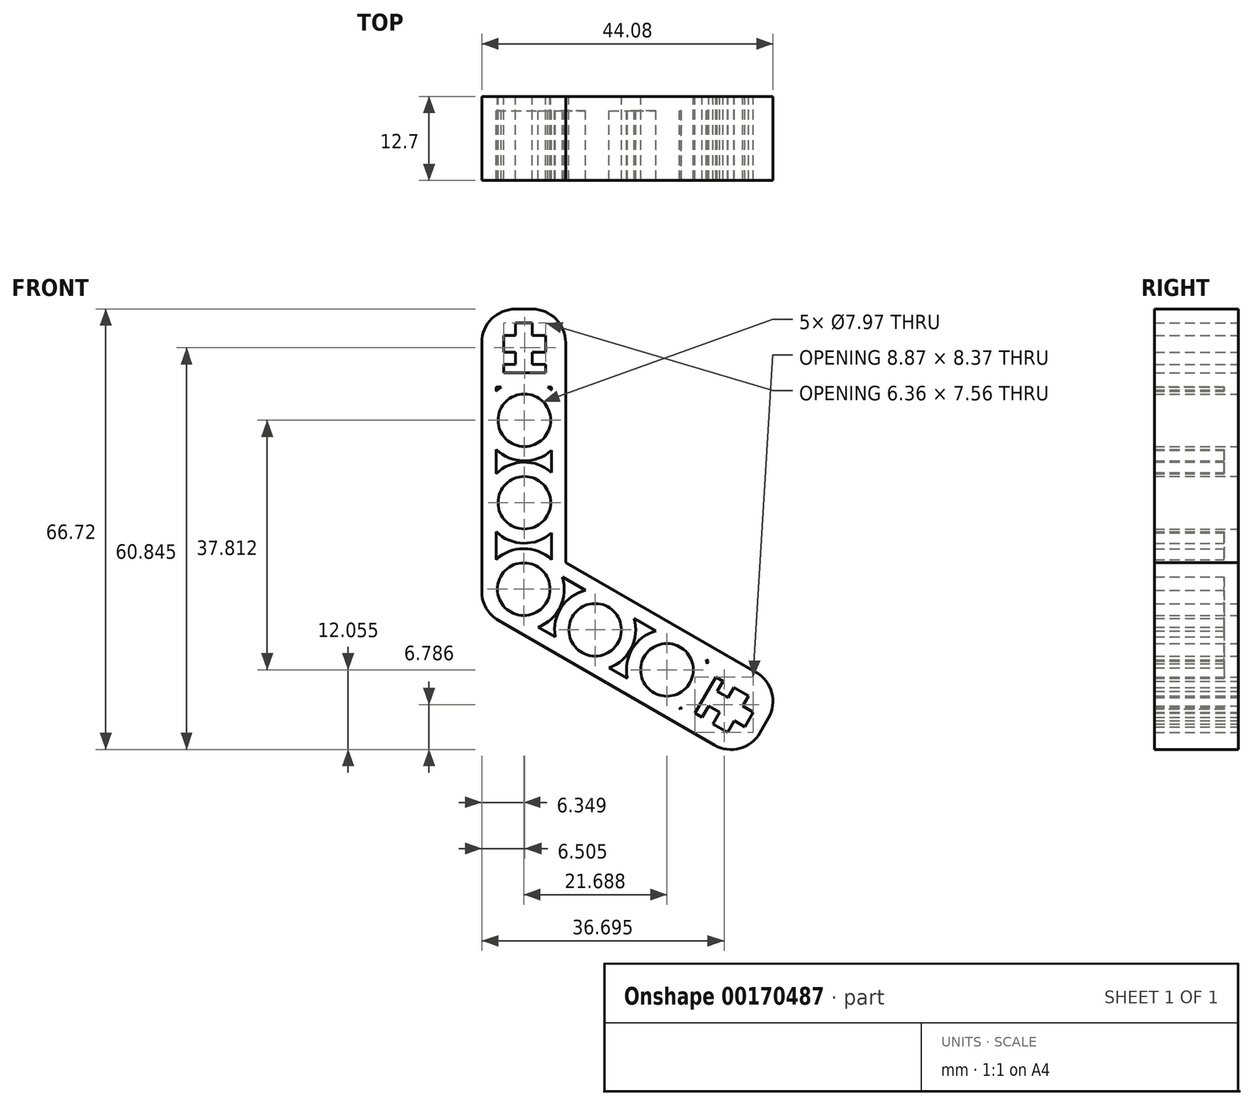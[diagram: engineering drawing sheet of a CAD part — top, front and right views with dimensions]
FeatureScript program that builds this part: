
annotation { "Feature Type Name" : "Feature", "Feature Type Description" : "" }
export const myFeature = defineFeature(function(context is Context, id is Id, definition is map)
    precondition{}
    {
        {
            var Q0;
            Q0=qCreatedBy(makeId("Front.planeOp"),FACE);
            var sketch = newSketch(context, id + "F0", { "sketchPlane" : qUnion([Q0])});
            skLineSegment(sketch, "E0.bottom", {"start": v(-54.24, 38.39) * mm, "end": v(-41.54, 38.39) * mm});
            skLineSegment(sketch, "E0.left", {"start": v(-54.24, 38.39) * mm, "end": v(-54.24, -7.33) * mm});
            skLineSegment(sketch, "E0.right", {"start": v(-41.54, 38.39) * mm, "end": v(-41.54, 0) * mm});
            skLineSegment(sketch, "E1.top", {"start": v(-14.65, -30.2) * mm, "end": v(-8.3, -19.2) * mm});
            skLineSegment(sketch, "E1.left", {"start": v(-54.24, -7.33) * mm, "end": v(-14.65, -30.2) * mm});
            skLineSegment(sketch, "E1.right", {"start": v(-41.54, 0) * mm, "end": v(-8.3, -19.2) * mm});
            skCircle(sketch, "E2", {"center": v(-47.9, -4.05) * mm, "radius": 3.98 * mm});
            skLineSegment(sketch, "E3.bottom", {"start": v(-16.05, -18.96) * mm, "end": v(-13.85, -20.24) * mm});
            skLineSegment(sketch, "E3.top", {"start": v(-19.23, -24.46) * mm, "end": v(-17.04, -25.73) * mm});
            skLineSegment(sketch, "E3.left", {"start": v(-16.05, -18.96) * mm, "end": v(-19.23, -24.46) * mm});
            skLineSegment(sketch, "E3.right", {"start": v(-13.85, -20.24) * mm, "end": v(-17.04, -25.73) * mm});
            skLineSegment(sketch, "E4.bottom", {"start": v(-19.88, -21.73) * mm, "end": v(-18.6, -19.53) * mm});
            skLineSegment(sketch, "E4.top", {"start": v(-14.39, -24.91) * mm, "end": v(-13.11, -22.72) * mm});
            skLineSegment(sketch, "E4.left", {"start": v(-19.88, -21.73) * mm, "end": v(-14.39, -24.91) * mm});
            skLineSegment(sketch, "E4.right", {"start": v(-18.6, -19.53) * mm, "end": v(-13.11, -22.72) * mm});
            skLineSegment(sketch, "E5.bottom", {"start": v(-18.8, -17.36) * mm, "end": v(-17.7, -18) * mm});
            skLineSegment(sketch, "E5.top", {"start": v(-21.98, -22.85) * mm, "end": v(-20.88, -23.49) * mm});
            skLineSegment(sketch, "E5.left", {"start": v(-18.8, -17.36) * mm, "end": v(-21.98, -22.85) * mm});
            skLineSegment(sketch, "E5.right", {"start": v(-17.7, -18) * mm, "end": v(-20.88, -23.49) * mm});
            skLineSegment(sketch, "E6.bottom", {"start": v(-50.92, 31.87) * mm, "end": v(-50.9, 34.41) * mm});
            skLineSegment(sketch, "E6.top", {"start": v(-44.57, 31.86) * mm, "end": v(-44.56, 34.4) * mm});
            skLineSegment(sketch, "E6.left", {"start": v(-50.92, 31.87) * mm, "end": v(-44.57, 31.86) * mm});
            skLineSegment(sketch, "E6.right", {"start": v(-50.9, 34.41) * mm, "end": v(-44.56, 34.4) * mm});
            skLineSegment(sketch, "E7.bottom", {"start": v(-46.6, 30.02) * mm, "end": v(-49.15, 30.03) * mm});
            skLineSegment(sketch, "E7.top", {"start": v(-46.6, 36.29) * mm, "end": v(-49.13, 36.3) * mm});
            skLineSegment(sketch, "E7.left", {"start": v(-46.6, 30.02) * mm, "end": v(-46.6, 36.29) * mm});
            skLineSegment(sketch, "E7.right", {"start": v(-49.15, 30.03) * mm, "end": v(-49.13, 36.3) * mm});
            skLineSegment(sketch, "E8.bottom", {"start": v(-50.9, 28.75) * mm, "end": v(-50.9, 30.03) * mm});
            skLineSegment(sketch, "E8.top", {"start": v(-44.56, 28.74) * mm, "end": v(-44.55, 30.02) * mm});
            skLineSegment(sketch, "E8.left", {"start": v(-50.9, 28.75) * mm, "end": v(-44.56, 28.74) * mm});
            skLineSegment(sketch, "E8.right", {"start": v(-50.9, 30.03) * mm, "end": v(-44.55, 30.02) * mm});
            skCircle(sketch, "E9", {"center": v(-37.08, -10.2) * mm, "radius": 3.98 * mm});
            skCircle(sketch, "E10", {"center": v(-47.8, 9.05) * mm, "radius": 3.98 * mm});
            skCircle(sketch, "E11", {"center": v(-47.8, 21.54) * mm, "radius": 3.98 * mm});
            skCircle(sketch, "E12", {"center": v(-26.2, -16.28) * mm, "radius": 3.98 * mm});
            skCircle(sketch, "E13", {"center": v(-47.8, 21.54) * mm, "radius": 4.75 * mm});
            skCircle(sketch, "E14", {"center": v(-47.8, 9.05) * mm, "radius": 4.75 * mm});
            skCircle(sketch, "E15", {"center": v(-47.9, -4.05) * mm, "radius": 4.75 * mm});
            skCircle(sketch, "E16", {"center": v(-37.08, -10.2) * mm, "radius": 4.75 * mm});
            skCircle(sketch, "E17", {"center": v(-26.2, -16.28) * mm, "radius": 4.75 * mm});
            skSolve(sketch);
        }
        {
            var Q0;
            Q0=makeQuery(id+"F0.imprint","IMPRINT",FACE,{"disambiguationData":[TD([[makeQuery(id+"F0.imprint","IMPRINT",EDGE,{"derivedFrom":sQuery(id+"F0.wireOp",EDGE,"E11")}),-1.0]])]});
            var Q1;
            Q1=makeQuery(id+"F0.imprint","IMPRINT",FACE,{"disambiguationData":[TD([[makeQuery(id+"F0.imprint","IMPRINT",EDGE,{"derivedFrom":sQuery(id+"F0.wireOp",EDGE,"E10")}),-1.0]])]});
            var Q2;
            Q2=makeQuery(id+"F0.imprint","IMPRINT",FACE,{"disambiguationData":[TD([[makeQuery(id+"F0.imprint","IMPRINT",EDGE,{"derivedFrom":sQuery(id+"F0.wireOp",EDGE,"E2")}),-1.0]])]});
            var Q3;
            Q3=makeQuery(id+"F0.imprint","IMPRINT",FACE,{"disambiguationData":[TD([[makeQuery(id+"F0.imprint","IMPRINT",EDGE,{"derivedFrom":sQuery(id+"F0.wireOp",EDGE,"E9")}),-1.0]])]});
            var Q4;
            Q4=makeQuery(id+"F0.imprint","IMPRINT",FACE,{"disambiguationData":[TD([[makeQuery(id+"F0.imprint","IMPRINT",EDGE,{"derivedFrom":sQuery(id+"F0.wireOp",EDGE,"E0.bottom")}),-1.0]])]});
            var Q5;
            Q5=makeQuery(id+"F0.imprint","IMPRINT",FACE,{"disambiguationData":[TD([[makeQuery(id+"F0.imprint","IMPRINT",EDGE,{"derivedFrom":sQuery(id+"F0.wireOp",EDGE,"E12")}),-1.0]])]});
            extrude(context, id + "F1", {"entities" : qUnion([Q0, Q1, Q2, Q3, Q4, Q5]), "depth" : 12.7 * mm});
        }
        {
            var Q0;
            Q0=makeQuery(id+"F1.opExtrude","SWEPT_EDGE",EDGE,{"disambiguationData":[OSD([sQuery(id+"F0.wireOp",EDGE,"E1.top"),sQuery(id+"F0.wireOp",EDGE,"E1.right")])]});
            fillet(context, id + "F2", {"entities" : qUnion([Q0]), "radius" : 5.08 * mm, "tangentPropagation" : true, "allowEdgeOverflow" : false});
        }
        {
            var Q0;
            Q0=makeQuery(id+"F1.opExtrude","SWEPT_EDGE",EDGE,{"disambiguationData":[OSD([sQuery(id+"F0.wireOp",EDGE,"E1.top"),sQuery(id+"F0.wireOp",EDGE,"E1.left")])]});
            fillet(context, id + "F3", {"entities" : qUnion([Q0]), "radius" : 5.08 * mm, "tangentPropagation" : true, "allowEdgeOverflow" : false});
        }
        {
            var Q0;
            Q0=makeQuery(id+"F1.opExtrude","SWEPT_EDGE",EDGE,{"disambiguationData":[OSD([sQuery(id+"F0.wireOp",EDGE,"E0.bottom"),sQuery(id+"F0.wireOp",EDGE,"E0.left")])]});
            fillet(context, id + "F4", {"entities" : qUnion([Q0]), "radius" : 5.08 * mm, "tangentPropagation" : true, "allowEdgeOverflow" : false});
        }
        {
            var Q0;
            Q0=makeQuery(id+"F1.opExtrude","SWEPT_EDGE",EDGE,{"disambiguationData":[OSD([sQuery(id+"F0.wireOp",EDGE,"E0.bottom"),sQuery(id+"F0.wireOp",EDGE,"E0.right")])]});
            fillet(context, id + "F5", {"entities" : qUnion([Q0]), "radius" : 5.08 * mm, "tangentPropagation" : true, "allowEdgeOverflow" : false});
        }
        {
            var Q0;
            Q0=makeQuery(id+"F1.opExtrude","SWEPT_EDGE",EDGE,{"disambiguationData":[OSD([sQuery(id+"F0.wireOp",EDGE,"E0.left"),sQuery(id+"F0.wireOp",EDGE,"E1.left")])]});
            fillet(context, id + "F6", {"entities" : qUnion([Q0]), "radius" : 5.08 * mm, "tangentPropagation" : true, "allowEdgeOverflow" : false});
        }
        {
            var Q0;
            Q0=makeQuery(id+"F1.opExtrude","CAP_FACE",FACE,{"disambiguationData":[OSD([sQuery(id+"F0.wireOp",EDGE,"E0.bottom"),sQuery(id+"F0.wireOp",EDGE,"E0.left"),sQuery(id+"F0.wireOp",EDGE,"E0.right"),sQuery(id+"F0.wireOp",EDGE,"E1.top"),sQuery(id+"F0.wireOp",EDGE,"E1.left"),sQuery(id+"F0.wireOp",EDGE,"E1.right"),sQuery(id+"F0.wireOp",EDGE,"E2"),sQuery(id+"F0.wireOp",EDGE,"E3.bottom"),sQuery(id+"F0.wireOp",EDGE,"E3.top"),sQuery(id+"F0.wireOp",EDGE,"E3.left"),sQuery(id+"F0.wireOp",EDGE,"E3.right"),sQuery(id+"F0.wireOp",EDGE,"E4.top"),sQuery(id+"F0.wireOp",EDGE,"E4.left"),sQuery(id+"F0.wireOp",EDGE,"E4.right"),sQuery(id+"F0.wireOp",EDGE,"E5.bottom"),sQuery(id+"F0.wireOp",EDGE,"E5.top"),sQuery(id+"F0.wireOp",EDGE,"E5.left"),sQuery(id+"F0.wireOp",EDGE,"E5.right"),sQuery(id+"F0.wireOp",EDGE,"E6.bottom"),sQuery(id+"F0.wireOp",EDGE,"E6.top"),sQuery(id+"F0.wireOp",EDGE,"E6.left"),sQuery(id+"F0.wireOp",EDGE,"E6.right"),sQuery(id+"F0.wireOp",EDGE,"E7.top"),sQuery(id+"F0.wireOp",EDGE,"E7.left"),sQuery(id+"F0.wireOp",EDGE,"E7.right"),sQuery(id+"F0.wireOp",EDGE,"E8.bottom"),sQuery(id+"F0.wireOp",EDGE,"E8.top"),sQuery(id+"F0.wireOp",EDGE,"E8.left"),sQuery(id+"F0.wireOp",EDGE,"E8.right"),sQuery(id+"F0.wireOp",EDGE,"E9"),sQuery(id+"F0.wireOp",EDGE,"E10"),sQuery(id+"F0.wireOp",EDGE,"E11"),sQuery(id+"F0.wireOp",EDGE,"E12")])],"isStart":false});
            shell(context, id + "F7", {"entities" : qUnion([Q0]), "thickness" : 2.16 * mm});
        }
    });
